FCSTD DOCUMENT  (FreeCAD 0.16RUnknown)
Label: 2d-open-box
License: All rights reserved
LicenseURL: http://en.wikipedia.org/wiki/All_rights_reserved
objects: Sketcher::SketchObject×5, Spreadsheet::Sheet×1
note: 5 computed .brp shape members not serialized (recipe doc carries the construction recipe); baked Part::Feature solids carry a one-line shape summary decoded from their .brp

FEATURE [Spreadsheet::Sheet] Spreadsheet  label="prefs"
  cells = A1=width; B1(width)=60; C1=mm; A2=depth; B2(depth)=40; C2=mm; A3=height; B3(height)=30; C3=mm; A4=thickness; B4(thickness)=3; C4=mm; A5=space; B5(space)=2; C5=mm
FEATURE [Sketcher::SketchObject] Sketch  label="bottom"
  expr: Constraints[50] = prefs.width - 2 * prefs.thickness
  expr: Constraints[51] = prefs.width
  expr: Constraints[21] = prefs.depth - 2 * prefs.thickness
  expr: Constraints[20] = prefs.depth - 2 * prefs.thickness
  expr: Constraints[22] = prefs.depth
  sketch-geometry (21):
    g0: LineSegment StartX=3 StartY=37 StartZ=0 EndX=21 EndY=37 EndZ=0
    g1: LineSegment StartX=21 StartY=37 StartZ=0 EndX=21 EndY=40 EndZ=0
    g2: LineSegment StartX=21 StartY=40 StartZ=0 EndX=39 EndY=40 EndZ=0
    g3: LineSegment StartX=39 StartY=40 StartZ=0 EndX=39 EndY=37 EndZ=0
    g4: LineSegment StartX=39 StartY=37 StartZ=0 EndX=57 EndY=37 EndZ=0
    g5: LineSegment StartX=57 StartY=37 StartZ=0 EndX=57 EndY=25.6667 EndZ=0
    g6: LineSegment StartX=57 StartY=25.6667 StartZ=0 EndX=60 EndY=25.6667 EndZ=0
    g7: LineSegment StartX=60 StartY=25.6667 StartZ=0 EndX=60 EndY=14.3333 EndZ=0
    g8: LineSegment StartX=60 StartY=14.3333 StartZ=0 EndX=57 EndY=14.3333 EndZ=0
    g9: LineSegment StartX=57 StartY=14.3333 StartZ=0 EndX=57 EndY=3 EndZ=0
    g10: LineSegment StartX=57 StartY=3 StartZ=0 EndX=39 EndY=3 EndZ=0
    g11: LineSegment StartX=39 StartY=3 StartZ=0 EndX=39 EndY=0 EndZ=0
    g12: LineSegment StartX=39 StartY=0 StartZ=0 EndX=21 EndY=0 EndZ=0
    g13: LineSegment StartX=21 StartY=0 StartZ=0 EndX=21 EndY=3 EndZ=0
    g14: LineSegment StartX=21 StartY=3 StartZ=0 EndX=3 EndY=3 EndZ=0
    g15: LineSegment StartX=3 StartY=3 StartZ=0 EndX=3 EndY=14.3333 EndZ=0
    g16: LineSegment StartX=3 StartY=14.3333 StartZ=0 EndX=0 EndY=14.3333 EndZ=0
    g17: LineSegment StartX=0 StartY=14.3333 StartZ=0 EndX=0 EndY=25.6667 EndZ=0
    g18: LineSegment StartX=0 StartY=25.6667 StartZ=0 EndX=3 EndY=25.6667 EndZ=0
    g19: LineSegment StartX=3 StartY=25.6667 StartZ=0 EndX=3 EndY=37 EndZ=0
    g20: GeomPoint [constr] X=-41.8758 Y=-31.3252 Z=0
  constraints (60):
    c: Coincident(g0,g1)
    c: Coincident(g1,g2)
    c: Coincident(g2,g3)
    c: Coincident(g3,g4)
    c: Coincident(g4,g5)
    c: Coincident(g5,g6)
    c: Coincident(g6,g7)
    c: Coincident(g7,g8)
    c: Coincident(g8,g9)
    c: Coincident(g9,g10)
    c: Coincident(g10,g11)
    c: Coincident(g11,g12)
    c: Coincident(g12,g13)
    c: Coincident(g13,g14)
    c: Coincident(g14,g15)
    c: Coincident(g15,g16)
    c: Coincident(g16,g17)
    c: Coincident(g17,g18)
    c: Coincident(g18,g19)
    c: Coincident(g19,g0)
    c: DistanceY(g9,g4) = 34
    c: DistanceY(g14,g0) = 34
    c: DistanceY(g12,g1) = 40
    c: Horizontal(g0)
    c: Horizontal(g2)
    c: Horizontal(g4)
    c: Horizontal(g10)
    c: Horizontal(g12)
    c: Horizontal(g14)
    c: Equal(g1,g13)
    c: Equal(g0,g2)
    c: Equal(g2,g4)
    c: Equal(g4,g10)
    c: Equal(g10,g12)
    c: Equal(g12,g14)
    c: Equal(g3,g11)
    c: Equal(g5,g7)
    c: Equal(g7,g9)
    c: Equal(g9,g19)
    c: Equal(g19,g17)
    c: Equal(g17,g15)
    c: Vertical(g3)
    c: Vertical(g1)
    c: Vertical(g13)
    c: Vertical(g11)
    c: Horizontal(g18)
    c: Horizontal(g16)
    c: Horizontal(g8)
    c: Equal(g18,g6)
    c: Equal(g16,g8)
    c: DistanceX(g0,g4) = 54
    c: DistanceX(g16,g7) = 60
    c: Vertical(g15)
    c: Vertical(g19)
    c: Vertical(g17)
    c: Vertical(g5)
    c: Vertical(g7)
    c: Vertical(g9)
    c: DistanceX(g-1,g16) = 0
    c: DistanceY(g12,g-1) = 0
FEATURE [Sketcher::SketchObject] Sketch001  label="front"
  Placement = pos=(0,42,0) rot=(0,0,1;0rad)
  expr: Constraints[47] = prefs.height - prefs.thickness
  expr: Constraints[46] = prefs.height
  expr: Constraints[32] = prefs.width - 2 * prefs.thickness
  expr: Constraints[43] = prefs.width - 2 * prefs.thickness
  expr: Placement.Base.y = prefs.depth + prefs.space
  expr: Constraints[33] = prefs.width
  sketch-geometry (17):
    g0: LineSegment StartX=3 StartY=30 StartZ=0 EndX=57 EndY=30 EndZ=0
    g1: LineSegment StartX=57 StartY=30 StartZ=0 EndX=57 EndY=20 EndZ=0
    g2: LineSegment StartX=57 StartY=20 StartZ=0 EndX=60 EndY=20 EndZ=0
    g3: LineSegment StartX=60 StartY=20 StartZ=0 EndX=60 EndY=9.99999 EndZ=0
    g4: LineSegment StartX=60 StartY=9.99999 StartZ=0 EndX=57 EndY=9.99999 EndZ=0
    g5: LineSegment StartX=57 StartY=9.99999 StartZ=0 EndX=57 EndY=-1.44613e-05 EndZ=0
    g6: LineSegment StartX=57 StartY=-1.44613e-05 StartZ=0 EndX=39 EndY=-1.44613e-05 EndZ=0
    g7: LineSegment StartX=39 StartY=-1.44613e-05 StartZ=0 EndX=39 EndY=3 EndZ=0
    g8: LineSegment StartX=39 StartY=3 StartZ=0 EndX=21 EndY=3 EndZ=0
    g9: LineSegment StartX=21 StartY=3 StartZ=0 EndX=21 EndY=0 EndZ=0
    g10: LineSegment StartX=21 StartY=0 StartZ=0 EndX=3 EndY=0 EndZ=0
    g11: LineSegment StartX=3 StartY=0 StartZ=0 EndX=3 EndY=10 EndZ=0
    g12: LineSegment StartX=3 StartY=10 StartZ=0 EndX=0 EndY=10 EndZ=0
    g13: LineSegment StartX=0 StartY=10 StartZ=0 EndX=0 EndY=20 EndZ=0
    g14: LineSegment StartX=0 StartY=20 StartZ=0 EndX=3 EndY=20 EndZ=0
    g15: LineSegment StartX=3 StartY=20 StartZ=0 EndX=3 EndY=30 EndZ=0
    g16: GeomPoint [constr] X=-41.8758 Y=-31.3252 Z=0
  constraints (48):
    c: Coincident(g0,g1)
    c: Coincident(g1,g2)
    c: Coincident(g2,g3)
    c: Coincident(g3,g4)
    c: Coincident(g4,g5)
    c: Coincident(g5,g6)
    c: Coincident(g6,g7)
    c: Coincident(g7,g8)
    c: Coincident(g8,g9)
    c: Coincident(g9,g10)
    c: Coincident(g10,g11)
    c: Coincident(g11,g12)
    c: Coincident(g12,g13)
    c: Coincident(g13,g14)
    c: Coincident(g14,g15)
    c: Horizontal(g0)
    c: Horizontal(g6)
    c: Horizontal(g8)
    c: Horizontal(g10)
    c: Equal(g6,g8)
    c: Equal(g8,g10)
    c: Equal(g1,g3)
    c: Equal(g3,g5)
    c: Equal(g5,g15)
    c: Equal(g15,g13)
    c: Equal(g13,g11)
    c: Vertical(g9)
    c: Vertical(g7)
    c: Horizontal(g14)
    c: Horizontal(g12)
    c: Horizontal(g4)
    c: Equal(g14,g2)
    c: DistanceX(g15,g0) = 54
    c: DistanceX(g12,g3) = 60
    c: Vertical(g11)
    c: Vertical(g15)
    c: Vertical(g13)
    c: Vertical(g1)
    c: Vertical(g3)
    c: Vertical(g5)
    c: DistanceX(g-1,g12) = 0
    c: DistanceY(g-1,g10) = 0
    c: Coincident(g0,g15)
    c: DistanceX(g10,g5) = 54
    c: Equal(g2,g4)
    c: Equal(g14,g12)
    c: DistanceY(g10,g0) = 30
    c: DistanceY(g8,g0) = 27
FEATURE [Sketcher::SketchObject] Sketch002  label="left"
  Placement = pos=(0,74,0) rot=(0,0,1;0rad)
  expr: Constraints[46] = prefs.height - prefs.thickness
  expr: Constraints[15] = prefs.height
  expr: Constraints[45] = prefs.depth
  expr: Constraints[16] = prefs.height
  expr: Constraints[41] = prefs.depth
  expr: Constraints[40] = prefs.depth - 2 * prefs.thickness
  expr: Placement.Base.y = prefs.depth + prefs.height + prefs.space * 2
  sketch-geometry (17):
    g0: LineSegment StartX=0 StartY=30 StartZ=0 EndX=40 EndY=30 EndZ=0
    g1: LineSegment StartX=40 StartY=30 StartZ=0 EndX=40 EndY=20 EndZ=0
    g2: LineSegment StartX=40 StartY=20 StartZ=0 EndX=37 EndY=20 EndZ=0
    g3: LineSegment StartX=37 StartY=20 StartZ=0 EndX=37 EndY=10 EndZ=0
    g4: LineSegment StartX=37 StartY=10 StartZ=0 EndX=40 EndY=10 EndZ=0
    g5: LineSegment StartX=40 StartY=10 StartZ=0 EndX=40 EndY=0 EndZ=0
    g6: LineSegment StartX=40 StartY=0 StartZ=0 EndX=26.6667 EndY=0 EndZ=0
    g7: LineSegment StartX=26.6667 StartY=0 StartZ=0 EndX=26.6667 EndY=3 EndZ=0
    g8: LineSegment StartX=26.6667 StartY=3 StartZ=0 EndX=13.3333 EndY=3 EndZ=0
    g9: LineSegment StartX=13.3333 StartY=3 StartZ=0 EndX=13.3333 EndY=0 EndZ=0
    g10: LineSegment StartX=13.3333 StartY=0 StartZ=0 EndX=0 EndY=0 EndZ=0
    g11: LineSegment StartX=0 StartY=0 StartZ=0 EndX=0 EndY=10 EndZ=0
    g12: LineSegment StartX=0 StartY=10 StartZ=0 EndX=3 EndY=10 EndZ=0
    g13: LineSegment StartX=3 StartY=10 StartZ=0 EndX=3 EndY=20 EndZ=0
    g14: LineSegment StartX=3 StartY=20 StartZ=0 EndX=0 EndY=20 EndZ=0
    g15: LineSegment StartX=0 StartY=20 StartZ=0 EndX=0 EndY=30 EndZ=0
    g16: GeomPoint [constr] X=-41.8758 Y=-31.3252 Z=0
  constraints (49):
    c: Coincident(g0,g1)
    c: Coincident(g1,g2)
    c: Coincident(g2,g3)
    c: Coincident(g3,g4)
    c: Coincident(g4,g5)
    c: Coincident(g5,g6)
    c: Coincident(g6,g7)
    c: Coincident(g7,g8)
    c: Coincident(g8,g9)
    c: Coincident(g9,g10)
    c: Coincident(g10,g11)
    c: Coincident(g11,g12)
    c: Coincident(g12,g13)
    c: Coincident(g13,g14)
    c: Coincident(g14,g15)
    c: DistanceY(g5,g0) = 30
    c: DistanceY(g10,g15) = 30
    c: Horizontal(g0)
    c: Horizontal(g6)
    c: Horizontal(g8)
    c: Horizontal(g10)
    c: Equal(g1,g3)
    c: Equal(g3,g5)
    c: Equal(g5,g15)
    c: Equal(g15,g13)
    c: Equal(g13,g11)
    c: Vertical(g9)
    c: Vertical(g7)
    c: Horizontal(g14)
    c: Horizontal(g12)
    c: Vertical(g11)
    c: Vertical(g15)
    c: Vertical(g13)
    c: Vertical(g1)
    c: Vertical(g3)
    c: Vertical(g5)
    c: DistanceY(g-1,g10) = 0
    c: Horizontal(g2)
    c: Equal(g14,g2)
    c: Equal(g12,g4)
    c: DistanceX(g13,g2) = 34
    c: DistanceX(g15,g0) = 40
    c: DistanceX(g-1,g10) = 0
    c: Equal(g10,g6)
    c: Coincident(g0,g15)
    c: DistanceX(g-1,g5) = 40
    c: DistanceY(g8,g0) = 27
    c: Equal(g10,g8)
    c: Equal(g8,g6)
FEATURE [Sketcher::SketchObject] Sketch004  label="back"
  Placement = pos=(62,42,0) rot=(0,0,1;0rad)
  expr: Constraints[15] = prefs.height
  expr: Constraints[47] = prefs.height - prefs.thickness
  expr: Constraints[46] = prefs.width - 2 * prefs.thickness
  expr: Placement.Base.x = prefs.width + prefs.space
  expr: Placement.Base.y = prefs.depth + prefs.space
  expr: Constraints[36] = prefs.width
  expr: Constraints[35] = prefs.width - 2 * prefs.thickness
  expr: Constraints[16] = prefs.height
  sketch-geometry (17):
    g0: LineSegment StartX=3 StartY=30 StartZ=0 EndX=57 EndY=30 EndZ=0
    g1: LineSegment StartX=57 StartY=30 StartZ=0 EndX=57 EndY=20 EndZ=0
    g2: LineSegment StartX=57 StartY=20 StartZ=0 EndX=60 EndY=20 EndZ=0
    g3: LineSegment StartX=60 StartY=20 StartZ=0 EndX=60 EndY=10 EndZ=0
    g4: LineSegment StartX=60 StartY=10 StartZ=0 EndX=57 EndY=10 EndZ=0
    g5: LineSegment StartX=57 StartY=10 StartZ=0 EndX=57 EndY=0 EndZ=0
    g6: LineSegment StartX=57 StartY=0 StartZ=0 EndX=39 EndY=0 EndZ=0
    g7: LineSegment StartX=39 StartY=0 StartZ=0 EndX=39 EndY=3 EndZ=0
    g8: LineSegment StartX=39 StartY=3 StartZ=0 EndX=21 EndY=3 EndZ=0
    g9: LineSegment StartX=21 StartY=3 StartZ=0 EndX=21 EndY=0 EndZ=0
    g10: LineSegment StartX=21 StartY=0 StartZ=0 EndX=3 EndY=0 EndZ=0
    g11: LineSegment StartX=3 StartY=0 StartZ=0 EndX=3 EndY=10 EndZ=0
    g12: LineSegment StartX=3 StartY=10 StartZ=0 EndX=0 EndY=10 EndZ=0
    g13: LineSegment StartX=0 StartY=10 StartZ=0 EndX=0 EndY=20 EndZ=0
    g14: LineSegment StartX=0 StartY=20 StartZ=0 EndX=3 EndY=20 EndZ=0
    g15: LineSegment StartX=3 StartY=20 StartZ=0 EndX=3 EndY=30 EndZ=0
    g16: GeomPoint [constr] X=-41.8758 Y=-31.3252 Z=0
  constraints (48):
    c: Coincident(g0,g1)
    c: Coincident(g1,g2)
    c: Coincident(g2,g3)
    c: Coincident(g3,g4)
    c: Coincident(g4,g5)
    c: Coincident(g5,g6)
    c: Coincident(g6,g7)
    c: Coincident(g7,g8)
    c: Coincident(g8,g9)
    c: Coincident(g9,g10)
    c: Coincident(g10,g11)
    c: Coincident(g11,g12)
    c: Coincident(g12,g13)
    c: Coincident(g13,g14)
    c: Coincident(g14,g15)
    c: DistanceY(g5,g0) = 30
    c: DistanceY(g10,g15) = 30
    c: Horizontal(g0)
    c: Horizontal(g6)
    c: Horizontal(g8)
    c: Horizontal(g10)
    c: Equal(g6,g8)
    c: Equal(g8,g10)
    c: Equal(g1,g3)
    c: Equal(g3,g5)
    c: Equal(g5,g15)
    c: Equal(g15,g13)
    c: Equal(g13,g11)
    c: Vertical(g9)
    c: Vertical(g7)
    c: Horizontal(g14)
    c: Horizontal(g12)
    c: Horizontal(g4)
    c: Equal(g14,g2)
    c: Equal(g12,g4)
    c: DistanceX(g15,g0) = 54
    c: DistanceX(g12,g3) = 60
    c: Vertical(g11)
    c: Vertical(g15)
    c: Vertical(g13)
    c: Vertical(g1)
    c: Vertical(g3)
    c: Vertical(g5)
    c: DistanceX(g-1,g12) = 0
    c: DistanceY(g-1,g10) = 0
    c: Coincident(g0,g15)
    c: DistanceX(g10,g5) = 54
    c: DistanceY(g8,g0) = 27
FEATURE [Sketcher::SketchObject] Sketch006  label="right"
  Placement = pos=(42,74,0) rot=(0,0,1;0rad)
  expr: Constraints[15] = prefs.height
  expr: Constraints[45] = prefs.height - prefs.thickness
  expr: Placement.Base.x = prefs.depth + prefs.space
  expr: Placement.Base.y = prefs.depth + prefs.height + prefs.space * 2
  expr: Constraints[48] = prefs.depth
  expr: Constraints[16] = prefs.height
  expr: Constraints[41] = prefs.depth
  expr: Constraints[40] = prefs.depth - 2 * prefs.thickness
  sketch-geometry (17):
    g0: LineSegment StartX=0 StartY=30 StartZ=0 EndX=40 EndY=30 EndZ=0
    g1: LineSegment StartX=40 StartY=30 StartZ=0 EndX=40 EndY=20 EndZ=0
    g2: LineSegment StartX=40 StartY=20 StartZ=0 EndX=37 EndY=20 EndZ=0
    g3: LineSegment StartX=37 StartY=20 StartZ=0 EndX=37 EndY=10 EndZ=0
    g4: LineSegment StartX=37 StartY=10 StartZ=0 EndX=40 EndY=10 EndZ=0
    g5: LineSegment StartX=40 StartY=10 StartZ=0 EndX=40 EndY=0 EndZ=0
    g6: LineSegment StartX=40 StartY=0 StartZ=0 EndX=26.6667 EndY=0 EndZ=0
    g7: LineSegment StartX=26.6667 StartY=0 StartZ=0 EndX=26.6667 EndY=3 EndZ=0
    g8: LineSegment StartX=26.6667 StartY=3 StartZ=0 EndX=13.3333 EndY=3 EndZ=0
    g9: LineSegment StartX=13.3333 StartY=3 StartZ=0 EndX=13.3333 EndY=0 EndZ=0
    g10: LineSegment StartX=13.3333 StartY=0 StartZ=0 EndX=0 EndY=0 EndZ=0
    g11: LineSegment StartX=0 StartY=0 StartZ=0 EndX=0 EndY=10 EndZ=0
    g12: LineSegment StartX=0 StartY=10 StartZ=0 EndX=3 EndY=10 EndZ=0
    g13: LineSegment StartX=3 StartY=10 StartZ=0 EndX=3 EndY=20 EndZ=0
    g14: LineSegment StartX=3 StartY=20 StartZ=0 EndX=0 EndY=20 EndZ=0
    g15: LineSegment StartX=0 StartY=20 StartZ=0 EndX=0 EndY=30 EndZ=0
    g16: GeomPoint [constr] X=-41.8758 Y=-31.3252 Z=0
  constraints (49):
    c: Coincident(g0,g1)
    c: Coincident(g1,g2)
    c: Coincident(g2,g3)
    c: Coincident(g3,g4)
    c: Coincident(g4,g5)
    c: Coincident(g5,g6)
    c: Coincident(g6,g7)
    c: Coincident(g7,g8)
    c: Coincident(g8,g9)
    c: Coincident(g9,g10)
    c: Coincident(g10,g11)
    c: Coincident(g11,g12)
    c: Coincident(g12,g13)
    c: Coincident(g13,g14)
    c: Coincident(g14,g15)
    c: DistanceY(g5,g0) = 30
    c: DistanceY(g10,g15) = 30
    c: Horizontal(g0)
    c: Horizontal(g6)
    c: Horizontal(g8)
    c: Horizontal(g10)
    c: Equal(g1,g3)
    c: Equal(g3,g5)
    c: Equal(g5,g15)
    c: Equal(g15,g13)
    c: Equal(g13,g11)
    c: Vertical(g9)
    c: Vertical(g7)
    c: Horizontal(g14)
    c: Horizontal(g12)
    c: Vertical(g11)
    c: Vertical(g15)
    c: Vertical(g13)
    c: Vertical(g1)
    c: Vertical(g3)
    c: Vertical(g5)
    c: DistanceY(g-1,g10) = 0
    c: Horizontal(g2)
    c: Equal(g14,g2)
    c: Equal(g12,g4)
    c: DistanceX(g13,g2) = 34
    c: DistanceX(g15,g0) = 40
    c: DistanceX(g-1,g10) = 0
    c: Equal(g10,g6)
    c: Coincident(g0,g15)
    c: DistanceY(g8,g0) = 27
    c: Equal(g10,g8)
    c: Equal(g8,g6)
    c: DistanceX(g-1,g5) = 40
